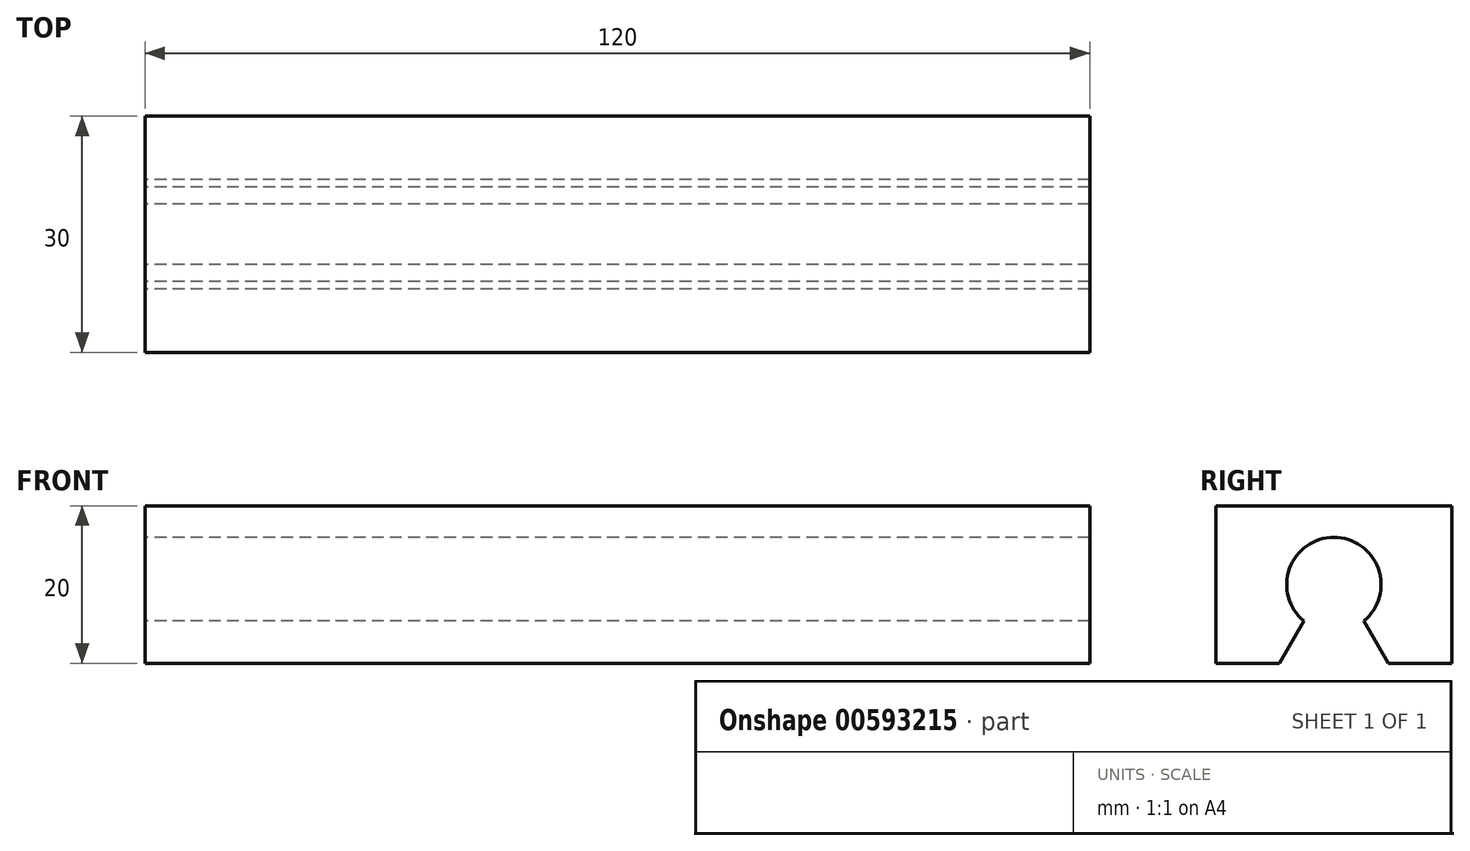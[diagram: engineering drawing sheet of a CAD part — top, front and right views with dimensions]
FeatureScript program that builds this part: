
annotation { "Feature Type Name" : "Feature", "Feature Type Description" : "" }
export const myFeature = defineFeature(function(context is Context, id is Id, definition is map)
    precondition{}
    {
        {
            var Q0;
            Q0=qCreatedBy(makeId("Right.planeOp"),FACE);
            var sketch = newSketch(context, id + "F0", { "sketchPlane" : qUnion([Q0])});
            skCircle(sketch, "E0", {"center": v(0, 0) * mm, "radius": 6 * mm});
            skLineSegment(sketch, "E1.bottom", {"start": v(-15, 10) * mm, "end": v(15, 10) * mm});
            skLineSegment(sketch, "E1.top", {"start": v(-15, -10) * mm, "end": v(15, -10) * mm});
            skLineSegment(sketch, "E1.left", {"start": v(-15, 10) * mm, "end": v(-15, -10) * mm});
            skLineSegment(sketch, "E1.right", {"start": v(15, 10) * mm, "end": v(15, -10) * mm});
            skPoint(sketch, "E2", {"position": v(0, 2) * mm});
            skPoint(sketch, "E3", {"position": v(0, -16) * mm});
            skLineSegment(sketch, "E4", {"start": v(0, 2) * mm, "end": v(-10.4, -16) * mm});
            skLineSegment(sketch, "E5.MirrorCS", {"start": v(0, 2) * mm, "end": v(10.4, -16) * mm});
            skSolve(sketch);
        }
        {
            var Q0;
            Q0=makeQuery(id+"F0.imprint","IMPRINT",FACE,{"disambiguationData":[TD([[makeQuery(id+"F0.imprint","IMPRINT",EDGE,{"derivedFrom":sQuery(id+"F0.wireOp",EDGE,"E1.bottom")}),-1.0]])]});
            extrude(context, id + "F1", {"entities" : qUnion([Q0]), "endBound" : BoundingType.SYMMETRIC, "depth" : 120 * mm, "offsetDistance" : 25 * mm});
        }
    });
